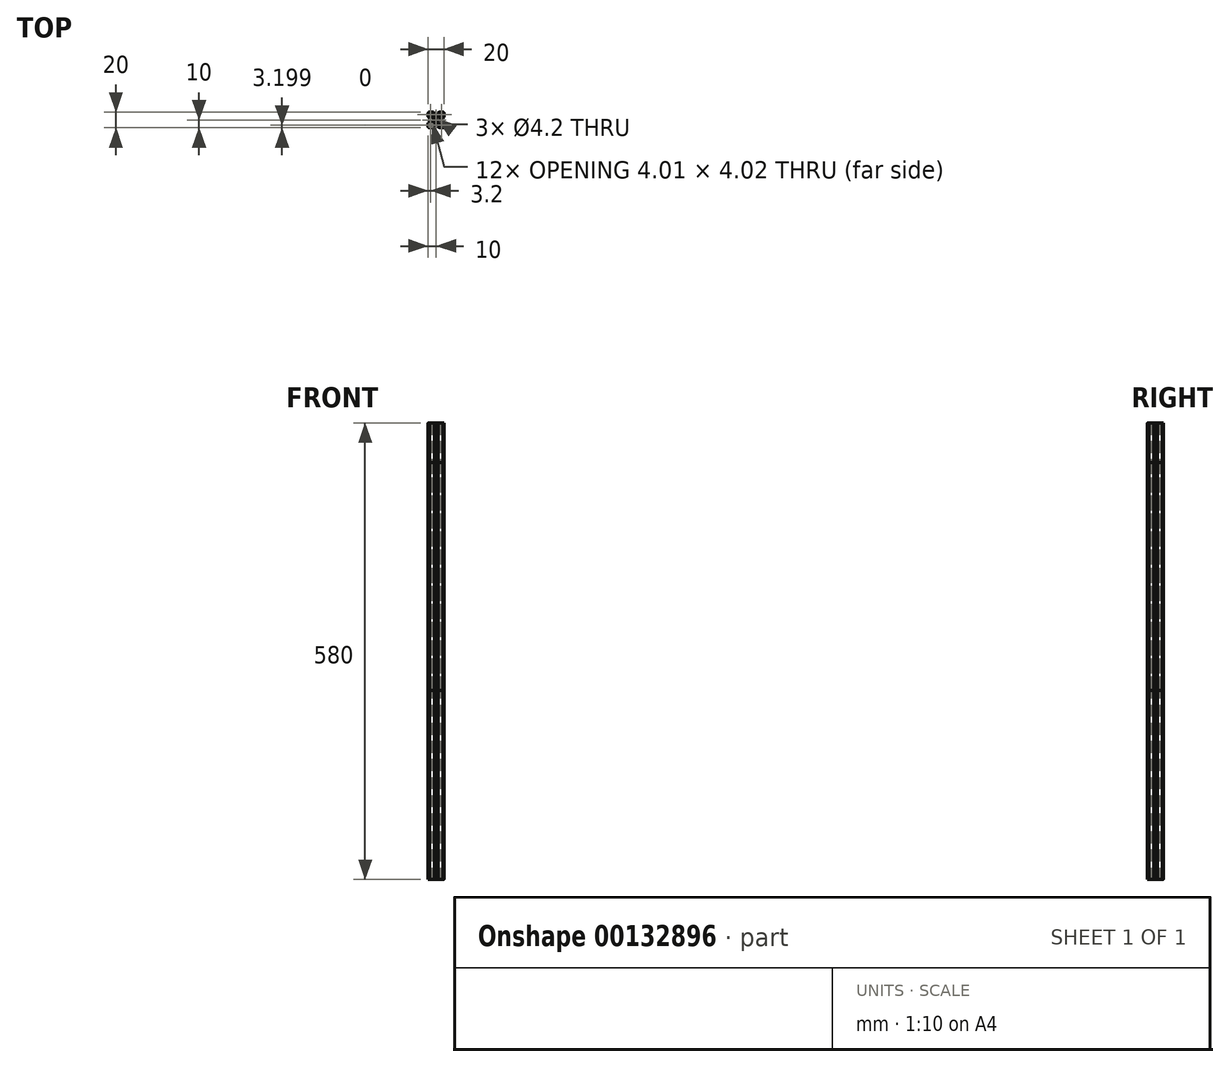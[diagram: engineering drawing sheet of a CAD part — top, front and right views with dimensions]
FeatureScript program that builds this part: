
annotation { "Feature Type Name" : "Feature", "Feature Type Description" : "" }
export const myFeature = defineFeature(function(context is Context, id is Id, definition is map)
    precondition{}
    {
        {
            var Q0;
            Q0=qCreatedBy(makeId("Top.planeOp"),FACE);
            var sketch = newSketch(context, id + "F0", { "sketchPlane" : qUnion([Q0])});
            skCircle(sketch, "E0", {"center": v(0, 0) * mm, "radius": 2.1 * mm});
            skArc(sketch, "E1", {"start": v(-5.39, -4.8) * mm, "mid": v(-4.94, -4.93) * mm, "end": v(-4.8, -5.38) * mm});
            skLineSegment(sketch, "E2", {"start": v(-5.39, -4.8) * mm, "end": v(-8.39, -4.8) * mm});
            skArc(sketch, "E3", {"start": v(-8.8, -5.38) * mm, "mid": v(-8.72, -5) * mm, "end": v(-8.39, -4.8) * mm});
            skLineSegment(sketch, "E4", {"start": v(-8.8, -5.38) * mm, "end": v(-8.8, -8.38) * mm});
            skArc(sketch, "E5", {"start": v(-8.4, -8.8) * mm, "mid": v(-8.67, -8.65) * mm, "end": v(-8.8, -8.38) * mm});
            skLineSegment(sketch, "E6", {"start": v(-8.4, -8.8) * mm, "end": v(-5.4, -8.8) * mm});
            skArc(sketch, "E7", {"start": v(-4.8, -8.38) * mm, "mid": v(-5, -8.72) * mm, "end": v(-5.4, -8.8) * mm});
            skLineSegment(sketch, "E8", {"start": v(-4.8, -8.38) * mm, "end": v(-4.8, -5.38) * mm});
            skArc(sketch, "E9", {"start": v(5.39, 4.8) * mm, "mid": v(4.94, 4.93) * mm, "end": v(4.8, 5.38) * mm});
            skLineSegment(sketch, "E10", {"start": v(5.39, 4.8) * mm, "end": v(8.39, 4.8) * mm});
            skArc(sketch, "E11", {"start": v(8.8, 5.38) * mm, "mid": v(8.72, 5) * mm, "end": v(8.39, 4.8) * mm});
            skLineSegment(sketch, "E12", {"start": v(8.8, 5.38) * mm, "end": v(8.8, 8.38) * mm});
            skArc(sketch, "E13", {"start": v(8.4, 8.8) * mm, "mid": v(8.67, 8.65) * mm, "end": v(8.8, 8.38) * mm});
            skLineSegment(sketch, "E14", {"start": v(8.4, 8.8) * mm, "end": v(5.4, 8.8) * mm});
            skArc(sketch, "E15", {"start": v(4.8, 8.38) * mm, "mid": v(5, 8.72) * mm, "end": v(5.4, 8.8) * mm});
            skLineSegment(sketch, "E16", {"start": v(4.8, 8.38) * mm, "end": v(4.8, 5.38) * mm});
            skLineSegment(sketch, "E17", {"start": v(8.8, -5.38) * mm, "end": v(8.8, -8.38) * mm});
            skArc(sketch, "E18", {"start": v(8.8, -5.38) * mm, "mid": v(8.72, -5) * mm, "end": v(8.39, -4.8) * mm});
            skLineSegment(sketch, "E19", {"start": v(5.39, -4.8) * mm, "end": v(8.39, -4.8) * mm});
            skArc(sketch, "E20", {"start": v(5.39, -4.8) * mm, "mid": v(4.94, -4.93) * mm, "end": v(4.8, -5.38) * mm});
            skLineSegment(sketch, "E21", {"start": v(4.8, -8.38) * mm, "end": v(4.8, -5.38) * mm});
            skArc(sketch, "E22", {"start": v(4.8, -8.38) * mm, "mid": v(5, -8.72) * mm, "end": v(5.4, -8.8) * mm});
            skLineSegment(sketch, "E23", {"start": v(8.4, -8.8) * mm, "end": v(5.4, -8.8) * mm});
            skArc(sketch, "E24", {"start": v(8.4, -8.8) * mm, "mid": v(8.67, -8.65) * mm, "end": v(8.8, -8.38) * mm});
            skLineSegment(sketch, "E25", {"start": v(-8.8, 5.38) * mm, "end": v(-8.8, 8.38) * mm});
            skArc(sketch, "E26", {"start": v(-8.8, 5.38) * mm, "mid": v(-8.72, 5) * mm, "end": v(-8.39, 4.8) * mm});
            skLineSegment(sketch, "E27", {"start": v(-5.39, 4.8) * mm, "end": v(-8.39, 4.8) * mm});
            skArc(sketch, "E28", {"start": v(-5.39, 4.8) * mm, "mid": v(-4.94, 4.93) * mm, "end": v(-4.8, 5.38) * mm});
            skLineSegment(sketch, "E29", {"start": v(-4.8, 8.38) * mm, "end": v(-4.8, 5.38) * mm});
            skArc(sketch, "E30", {"start": v(-4.8, 8.38) * mm, "mid": v(-5, 8.72) * mm, "end": v(-5.4, 8.8) * mm});
            skLineSegment(sketch, "E31", {"start": v(-8.4, 8.8) * mm, "end": v(-5.4, 8.8) * mm});
            skArc(sketch, "E32", {"start": v(-8.4, 8.8) * mm, "mid": v(-8.67, 8.65) * mm, "end": v(-8.8, 8.38) * mm});
            skArc(sketch, "E33", {"start": v(-10, -4.25) * mm, "mid": v(-9.94, -3.95) * mm, "end": v(-9.77, -3.7) * mm});
            skLineSegment(sketch, "E34", {"start": v(-9.77, -3.7) * mm, "end": v(-8.49, -2.4) * mm});
            skArc(sketch, "E35", {"start": v(-8.49, -2.4) * mm, "mid": v(-8.27, -2.36) * mm, "end": v(-8.14, -2.54) * mm});
            skLineSegment(sketch, "E36", {"start": v(-8.14, -2.54) * mm, "end": v(-8.14, -3.6) * mm});
            skLineSegment(sketch, "E37", {"start": v(-8.14, -3.6) * mm, "end": v(-5.03, -3.6) * mm});
            skLineSegment(sketch, "E38", {"start": v(-5.03, -3.6) * mm, "end": v(-3.4, -1.97) * mm});
            skLineSegment(sketch, "E39", {"start": v(-3.4, -1.97) * mm, "end": v(-3.4, -0.38) * mm});
            skLineSegment(sketch, "E40", {"start": v(-3.4, -0.38) * mm, "end": v(-3.02, 0) * mm});
            skLineSegment(sketch, "E41", {"start": v(-3.4, 0.38) * mm, "end": v(-3.02, 0) * mm});
            skLineSegment(sketch, "E42", {"start": v(-3.4, 1.97) * mm, "end": v(-3.4, 0.38) * mm});
            skLineSegment(sketch, "E43", {"start": v(-5.03, 3.6) * mm, "end": v(-3.4, 1.97) * mm});
            skLineSegment(sketch, "E44", {"start": v(-8.14, 3.6) * mm, "end": v(-5.03, 3.6) * mm});
            skLineSegment(sketch, "E45", {"start": v(-8.14, 2.54) * mm, "end": v(-8.14, 3.6) * mm});
            skArc(sketch, "E46", {"start": v(-8.49, 2.4) * mm, "mid": v(-8.27, 2.36) * mm, "end": v(-8.14, 2.54) * mm});
            skLineSegment(sketch, "E47", {"start": v(-9.77, 3.7) * mm, "end": v(-8.49, 2.4) * mm});
            skArc(sketch, "E48", {"start": v(-10, 4.25) * mm, "mid": v(-9.94, 3.95) * mm, "end": v(-9.77, 3.7) * mm});
            skLineSegment(sketch, "E49", {"start": v(-10, 8.58) * mm, "end": v(-10, 4.25) * mm});
            skArc(sketch, "E50", {"start": v(-8.6, 10) * mm, "mid": v(-9.57, 9.56) * mm, "end": v(-10, 8.58) * mm});
            skLineSegment(sketch, "E51", {"start": v(-4.04, 10) * mm, "end": v(-8.6, 10) * mm});
            skArc(sketch, "E52", {"start": v(-3.48, 9.77) * mm, "mid": v(-3.74, 9.94) * mm, "end": v(-4.04, 10) * mm});
            skLineSegment(sketch, "E53", {"start": v(-2.37, 8.66) * mm, "end": v(-3.48, 9.77) * mm});
            skArc(sketch, "E54", {"start": v(-2.55, 8.23) * mm, "mid": v(-2.32, 8.39) * mm, "end": v(-2.37, 8.66) * mm});
            skLineSegment(sketch, "E55", {"start": v(-3.6, 8.23) * mm, "end": v(-2.55, 8.23) * mm});
            skLineSegment(sketch, "E56", {"start": v(-3.6, 5.03) * mm, "end": v(-3.6, 8.23) * mm});
            skLineSegment(sketch, "E57", {"start": v(-2, 3.43) * mm, "end": v(-3.6, 5.03) * mm});
            skLineSegment(sketch, "E58", {"start": v(-0.3, 3.43) * mm, "end": v(-2, 3.43) * mm});
            skLineSegment(sketch, "E59", {"start": v(0, 3.18) * mm, "end": v(-0.3, 3.43) * mm});
            skLineSegment(sketch, "E60", {"start": v(0, 3.18) * mm, "end": v(0.3, 3.43) * mm});
            skLineSegment(sketch, "E61", {"start": v(0.3, 3.43) * mm, "end": v(2, 3.43) * mm});
            skLineSegment(sketch, "E62", {"start": v(2, 3.43) * mm, "end": v(3.6, 5.03) * mm});
            skLineSegment(sketch, "E63", {"start": v(3.6, 5.03) * mm, "end": v(3.6, 8.23) * mm});
            skLineSegment(sketch, "E64", {"start": v(3.6, 8.23) * mm, "end": v(2.55, 8.23) * mm});
            skArc(sketch, "E65", {"start": v(2.55, 8.23) * mm, "mid": v(2.32, 8.39) * mm, "end": v(2.37, 8.66) * mm});
            skLineSegment(sketch, "E66", {"start": v(2.37, 8.66) * mm, "end": v(3.48, 9.77) * mm});
            skArc(sketch, "E67", {"start": v(3.48, 9.77) * mm, "mid": v(3.74, 9.94) * mm, "end": v(4.04, 10) * mm});
            skLineSegment(sketch, "E68", {"start": v(4.04, 10) * mm, "end": v(8.6, 10) * mm});
            skArc(sketch, "E69", {"start": v(8.6, 10) * mm, "mid": v(9.57, 9.56) * mm, "end": v(10, 8.58) * mm});
            skLineSegment(sketch, "E70", {"start": v(10, 8.58) * mm, "end": v(10, 4.25) * mm});
            skArc(sketch, "E71", {"start": v(10, 4.25) * mm, "mid": v(9.94, 3.95) * mm, "end": v(9.77, 3.7) * mm});
            skLineSegment(sketch, "E72", {"start": v(9.77, 3.7) * mm, "end": v(8.49, 2.4) * mm});
            skArc(sketch, "E73", {"start": v(8.49, 2.4) * mm, "mid": v(8.27, 2.36) * mm, "end": v(8.14, 2.54) * mm});
            skLineSegment(sketch, "E74", {"start": v(8.14, 2.54) * mm, "end": v(8.14, 3.6) * mm});
            skLineSegment(sketch, "E75", {"start": v(8.14, 3.6) * mm, "end": v(5.03, 3.6) * mm});
            skLineSegment(sketch, "E76", {"start": v(5.03, 3.6) * mm, "end": v(3.4, 1.97) * mm});
            skLineSegment(sketch, "E77", {"start": v(3.4, 1.97) * mm, "end": v(3.4, 0.38) * mm});
            skLineSegment(sketch, "E78", {"start": v(3.4, 0.38) * mm, "end": v(3.02, 0) * mm});
            skLineSegment(sketch, "E79", {"start": v(3.4, -0.38) * mm, "end": v(3.02, 0) * mm});
            skLineSegment(sketch, "E80", {"start": v(3.4, -1.97) * mm, "end": v(3.4, -0.38) * mm});
            skLineSegment(sketch, "E81", {"start": v(5.03, -3.6) * mm, "end": v(3.4, -1.97) * mm});
            skLineSegment(sketch, "E82", {"start": v(8.14, -3.6) * mm, "end": v(5.03, -3.6) * mm});
            skLineSegment(sketch, "E83", {"start": v(8.14, -2.54) * mm, "end": v(8.14, -3.6) * mm});
            skArc(sketch, "E84", {"start": v(8.49, -2.4) * mm, "mid": v(8.27, -2.36) * mm, "end": v(8.14, -2.54) * mm});
            skLineSegment(sketch, "E85", {"start": v(9.77, -3.7) * mm, "end": v(8.49, -2.4) * mm});
            skArc(sketch, "E86", {"start": v(10, -4.25) * mm, "mid": v(9.94, -3.95) * mm, "end": v(9.77, -3.7) * mm});
            skLineSegment(sketch, "E87", {"start": v(10, -8.58) * mm, "end": v(10, -4.25) * mm});
            skArc(sketch, "E88", {"start": v(8.6, -10) * mm, "mid": v(9.57, -9.56) * mm, "end": v(10, -8.58) * mm});
            skLineSegment(sketch, "E89", {"start": v(4.04, -10) * mm, "end": v(8.6, -10) * mm});
            skArc(sketch, "E90", {"start": v(3.48, -9.77) * mm, "mid": v(3.74, -9.94) * mm, "end": v(4.04, -10) * mm});
            skLineSegment(sketch, "E91", {"start": v(2.37, -8.66) * mm, "end": v(3.48, -9.77) * mm});
            skArc(sketch, "E92", {"start": v(2.55, -8.23) * mm, "mid": v(2.32, -8.39) * mm, "end": v(2.37, -8.66) * mm});
            skLineSegment(sketch, "E93", {"start": v(3.6, -8.23) * mm, "end": v(2.55, -8.23) * mm});
            skLineSegment(sketch, "E94", {"start": v(3.6, -5.03) * mm, "end": v(3.6, -8.23) * mm});
            skLineSegment(sketch, "E95", {"start": v(2, -3.43) * mm, "end": v(3.6, -5.03) * mm});
            skLineSegment(sketch, "E96", {"start": v(0.3, -3.43) * mm, "end": v(2, -3.43) * mm});
            skLineSegment(sketch, "E97", {"start": v(0, -3.18) * mm, "end": v(0.3, -3.43) * mm});
            skLineSegment(sketch, "E98", {"start": v(0, -3.18) * mm, "end": v(-0.3, -3.43) * mm});
            skLineSegment(sketch, "E99", {"start": v(-0.3, -3.43) * mm, "end": v(-2, -3.43) * mm});
            skLineSegment(sketch, "E100", {"start": v(-2, -3.43) * mm, "end": v(-3.6, -5.03) * mm});
            skLineSegment(sketch, "E101", {"start": v(-3.6, -5.03) * mm, "end": v(-3.6, -8.23) * mm});
            skLineSegment(sketch, "E102", {"start": v(-3.6, -8.23) * mm, "end": v(-2.55, -8.23) * mm});
            skArc(sketch, "E103", {"start": v(-2.55, -8.23) * mm, "mid": v(-2.32, -8.39) * mm, "end": v(-2.37, -8.66) * mm});
            skLineSegment(sketch, "E104", {"start": v(-2.37, -8.66) * mm, "end": v(-3.48, -9.77) * mm});
            skArc(sketch, "E105", {"start": v(-3.48, -9.77) * mm, "mid": v(-3.74, -9.94) * mm, "end": v(-4.04, -10) * mm});
            skLineSegment(sketch, "E106", {"start": v(-4.04, -10) * mm, "end": v(-8.6, -10) * mm});
            skArc(sketch, "E107", {"start": v(-8.6, -10) * mm, "mid": v(-9.57, -9.56) * mm, "end": v(-10, -8.58) * mm});
            skLineSegment(sketch, "E108", {"start": v(-10, -8.58) * mm, "end": v(-10, -4.25) * mm});
            skSolve(sketch);
        }
        {
            var Q0;
            Q0 = qSketchRegion(id + "F0", true);
            extrude(context, id + "F1", {"entities" : qUnion([Q0]), "depth" : 340 * mm});
        }
        {
            var Q0;
            Q0 = qSketchRegion(id + "F0", true);
            extrude(context, id + "F2", {"entities" : qUnion([Q0]), "oppositeDirection" : true, "depth" : 240 * mm});
        }
        {
            var Q0;
            Q0 = qSketchRegion(id + "F0", true);
            extrude(context, id + "F3", {"entities" : qUnion([Q0]), "depth" : 290 * mm});
        }
    });
